# Revit family: result
name_source: partatom
category: Lighting Fixtures
revit_build: Autodesk Revit 2015 (Build: 20140903_1530(x64)
units: mm (PartAtom-declared; Revit-internal decimal feet)

## types (1)
- Default
    BIMobject category = Pendant Lighting
    BIMobject category code = lighting-pendants
    BIMobject main category = Lighting
    BIMobject main category code = lighting
    Brand url = https://www.moltoluce.com
    Color Filter = 16777215
    Date of publishing = 2/16/2021
    Design country = Austria
    Dimming Lamp Color Temperature Shift = <None>
    Edition number = 1
    IFC Classification = Lamp
    Installation instructions = https://www.moltoluce.com
    Light Source Symbol Size = 609.6 mm  [stored 2 ft]
    Manufacturer country = Austria
    Manufacturer name = Molto Luce
    Masterformat 2014 Code = 26 50 00
    Masterformat 2014 Description = Lighting
    Material main = Aluminium
    Material secondary = Acrylic
    NBS Reference Code = 49
    NBS Reference Description = Luminaires And Lamps
    OmniClass Code = 23-35 45 15
    OmniClass Description = Lamps
    Product Guid = 0af18160-d901-41be-88f3-07dfe6ba508c
    Product SKU = System011_pendant_lamp
    Product data url = https://bimobject.com
    Product family = Lighting
    Product group = Pendant Lamp
    Product name = SYSTEM01.1 Pendant
    Product url = https://www.moltoluce.com
    QR code = http://bimobject.com
    UNSPSC Code = 3911
    Uniclass 1.4 Code = JY73
    Uniclass 1.4 Description = Luminaires and lamps
    Uniclass 2.0 Code = PR-49
    Uniclass 2.0 Description = Luminaires And Lamps
    Uniclass 2015 Code = Pr_70_70_48
    Uniclass 2015 Name = Luminaires, lighting track and lighting accessories
    Uniformat II Code = D5020
    Uniformat II Description = Lighting & Branch Wiring

note: [stored X ft] marks values corroborated as IEEE doubles in the binary element streams (Revit-internal decimal feet)

## geometry (parser evidence)
native form markers: Extrusion x7, Sweep x65
no freeform markers — native parametric forms only
